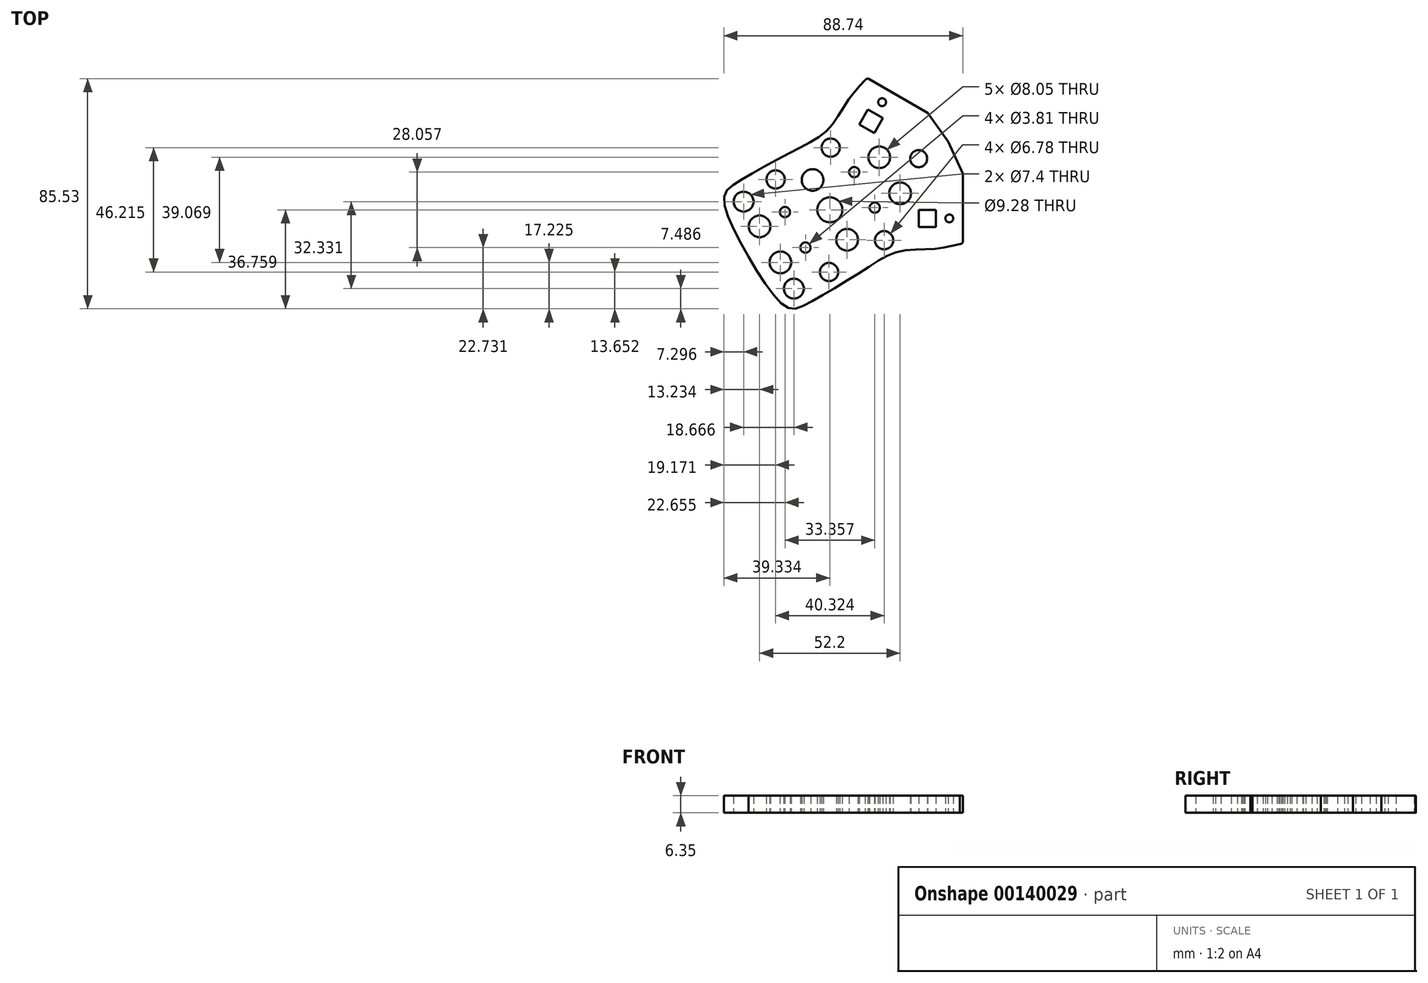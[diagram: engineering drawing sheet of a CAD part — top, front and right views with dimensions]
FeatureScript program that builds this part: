
annotation { "Feature Type Name" : "Feature", "Feature Type Description" : "" }
export const myFeature = defineFeature(function(context is Context, id is Id, definition is map)
    precondition{}
    {
        {
            var Q0;
            Q0=qCreatedBy(makeId("Top.planeOp"),FACE);
            var sketch = newSketch(context, id + "F0", { "sketchPlane" : qUnion([Q0])});
            skLineSegment(sketch, "E0.0", {"start": v(-166.81, -70.9) * mm, "end": v(-163.64, -65.4) * mm, "construction": true});
            skCircle(sketch, "E1", {"center": v(-144.81, -83.61) * mm, "radius": 3.18 * mm});
            skLineSegment(sketch, "E2", {"start": v(-144.81, -83.61) * mm, "end": v(-133.8, -77.26) * mm, "construction": true});
            skLineSegment(sketch, "E3", {"start": v(-161.31, -74.07) * mm, "end": v(-166.81, -70.9) * mm});
            skLineSegment(sketch, "E4", {"start": v(-161.31, -74.07) * mm, "end": v(-144.81, -83.61) * mm, "construction": true});
            skLineSegment(sketch, "E5", {"start": v(-166.81, -70.9) * mm, "end": v(-163.64, -65.4) * mm});
            skPoint(sketch, "E6.visualSharp", {"position": v(-164.26, -53.69) * mm});
            skArc(sketch, "E6.filletArc", {"start": v(-163.42, -53.93) * mm, "mid": v(-164.13, -53.98) * mm, "end": v(-164.64, -54.47) * mm});
            skPoint(sketch, "E7.visualSharp", {"position": v(-128.63, -115.42) * mm});
            skArc(sketch, "E7.filletArc", {"start": v(-129.49, -115.35) * mm, "mid": v(-128.8, -115.16) * mm, "end": v(-128.41, -114.57) * mm});
            skLineSegment(sketch, "E8.MirrorCS", {"start": v(-144.8, -102.67) * mm, "end": v(-144.8, -109.02) * mm});
            skLineSegment(sketch, "E9", {"start": v(-144.8, -102.67) * mm, "end": v(-138.45, -102.67) * mm});
            skLineSegment(sketch, "E10.MirrorCS", {"start": v(-138.45, -102.67) * mm, "end": v(-138.45, -109) * mm});
            skLineSegment(sketch, "E11", {"start": v(-163.42, -53.93) * mm, "end": v(-141.42, -66.62) * mm});
            skLineSegment(sketch, "E12", {"start": v(-141.42, -66.62) * mm, "end": v(-133.8, -77.26) * mm});
            skLineSegment(sketch, "E13.MirrorCS", {"start": v(-128.4, -89.17) * mm, "end": v(-133.8, -77.26) * mm});
            skLineSegment(sketch, "E14.MirrorCS", {"start": v(-128.41, -114.57) * mm, "end": v(-128.4, -89.17) * mm});
            skLineSegment(sketch, "E15", {"start": v(-144.8, -109.02) * mm, "end": v(-138.45, -109) * mm});
            skLineSegment(sketch, "E16.trimOffspring", {"start": v(-163.64, -65.4) * mm, "end": v(-166.81, -70.9) * mm});
            skLineSegment(sketch, "E17", {"start": v(-161.31, -74.07) * mm, "end": v(-158.14, -68.57) * mm});
            skLineSegment(sketch, "E18", {"start": v(-138.45, -105.84) * mm, "end": v(-128.4, -105.84) * mm, "construction": true});
            skCircle(sketch, "E19", {"center": v(-133.43, -105.84) * mm, "radius": 1.46 * mm});
            skCircle(sketch, "E20.MirrorC", {"center": v(-158.37, -62.64) * mm, "radius": 1.46 * mm});
            skLineSegment(sketch, "E21", {"start": v(-144.81, -83.61) * mm, "end": v(-147.56, -85.2) * mm, "construction": true});
            skLineSegment(sketch, "E22", {"start": v(-147.56, -85.2) * mm, "end": v(-208.05, -120.12) * mm, "construction": true});
            skLineSegment(sketch, "E23", {"start": v(-177.8, -102.66) * mm, "end": v(-164.98, -124.88) * mm, "construction": true});
            skLineSegment(sketch, "E24.MirrorCS", {"start": v(-177.8, -102.66) * mm, "end": v(-190.63, -80.44) * mm, "construction": true});
            skFitSpline(sketch, "E25", {"points": [v(-164.64, -54.47) * mm, v(-171.03, -61.87) * mm, v(-178.44, -72.71) * mm, v(-190.63, -80.44) * mm, v(-211.76, -92.13) * mm, v(-217.12, -98.26) * mm, v(-208.05, -120.12) * mm], "startDerivative": vector(-48.5, -49.6) * mm, "endDerivative": vector(67.55, -122.64) * mm});
            skFitSpline(sketch, "E26.MirrorCS", {"points": [v(-129.49, -115.35) * mm, v(-139.09, -117.19) * mm, v(-152.19, -118.18) * mm, v(-164.98, -124.88) * mm, v(-185.67, -137.33) * mm, v(-193.66, -138.9) * mm, v(-208.05, -120.12) * mm], "startDerivative": vector(-67.2, -17.2) * mm, "endDerivative": vector(-72.43, 119.82) * mm});
            skCircle(sketch, "E27", {"center": v(-209.84, -99.6) * mm, "radius": 3.7 * mm});
            skCircle(sketch, "E28", {"center": v(-203.9, -108.8) * mm, "radius": 4.03 * mm});
            skCircle(sketch, "E29", {"center": v(-197.97, -91.37) * mm, "radius": 3.39 * mm});
            skCircle(sketch, "E30.MirrorC", {"center": v(-196.17, -122.2) * mm, "radius": 4.03 * mm});
            skCircle(sketch, "E31.MirrorC", {"center": v(-191.18, -131.93) * mm, "radius": 3.7 * mm});
            skCircle(sketch, "E32.MirrorC", {"center": v(-178.1, -125.77) * mm, "radius": 3.39 * mm});
            skCircle(sketch, "E33.MirrorC", {"center": v(-177.5, -79.55) * mm, "radius": 3.39 * mm});
            skCircle(sketch, "E34.MirrorC", {"center": v(-159.44, -83.13) * mm, "radius": 4.03 * mm});
            skCircle(sketch, "E35.MirrorC", {"center": v(-151.7, -96.52) * mm, "radius": 4.03 * mm});
            skCircle(sketch, "E36.MirrorC", {"center": v(-157.64, -113.95) * mm, "radius": 3.39 * mm});
            skCircle(sketch, "E37", {"center": v(-177.8, -102.66) * mm, "radius": 4.64 * mm});
            skCircle(sketch, "E38", {"center": v(-184.22, -91.55) * mm, "radius": 4.02 * mm});
            skCircle(sketch, "E39", {"center": v(-171.4, -113.77) * mm, "radius": 4.03 * mm});
            skLineSegment(sketch, "E40", {"start": v(-163.64, -65.4) * mm, "end": v(-158.14, -68.57) * mm});
            skLineSegment(sketch, "E41.0", {"start": v(-164.94, -95.23) * mm, "end": v(-177.77, -73.01) * mm, "construction": true});
            skLineSegment(sketch, "E42.0", {"start": v(-151.37, -78.6) * mm, "end": v(-211.86, -113.52) * mm, "construction": true});
            skCircle(sketch, "E43", {"center": v(-168.75, -88.63) * mm, "radius": 1.9 * mm});
            skCircle(sketch, "E44.MirrorC", {"center": v(-161.13, -101.83) * mm, "radius": 1.9 * mm});
            skCircle(sketch, "E45.MirrorC", {"center": v(-186.86, -116.69) * mm, "radius": 1.9 * mm});
            skCircle(sketch, "E46.MirrorC", {"center": v(-194.48, -103.5) * mm, "radius": 1.9 * mm});
            skSolve(sketch);
        }
        {
            var Q0;
            Q0=makeQuery(id+"F0.imprint","IMPRINT",FACE,{"disambiguationData":[TD([[makeQuery(id+"F0.imprint","IMPRINT",EDGE,{"derivedFrom":sQuery(id+"F0.wireOp",EDGE,"E1")}),-1.0]])]});
            extrude(context, id + "F1", {"entities" : qUnion([Q0]), "depth" : 6.35 * mm});
        }
    });
